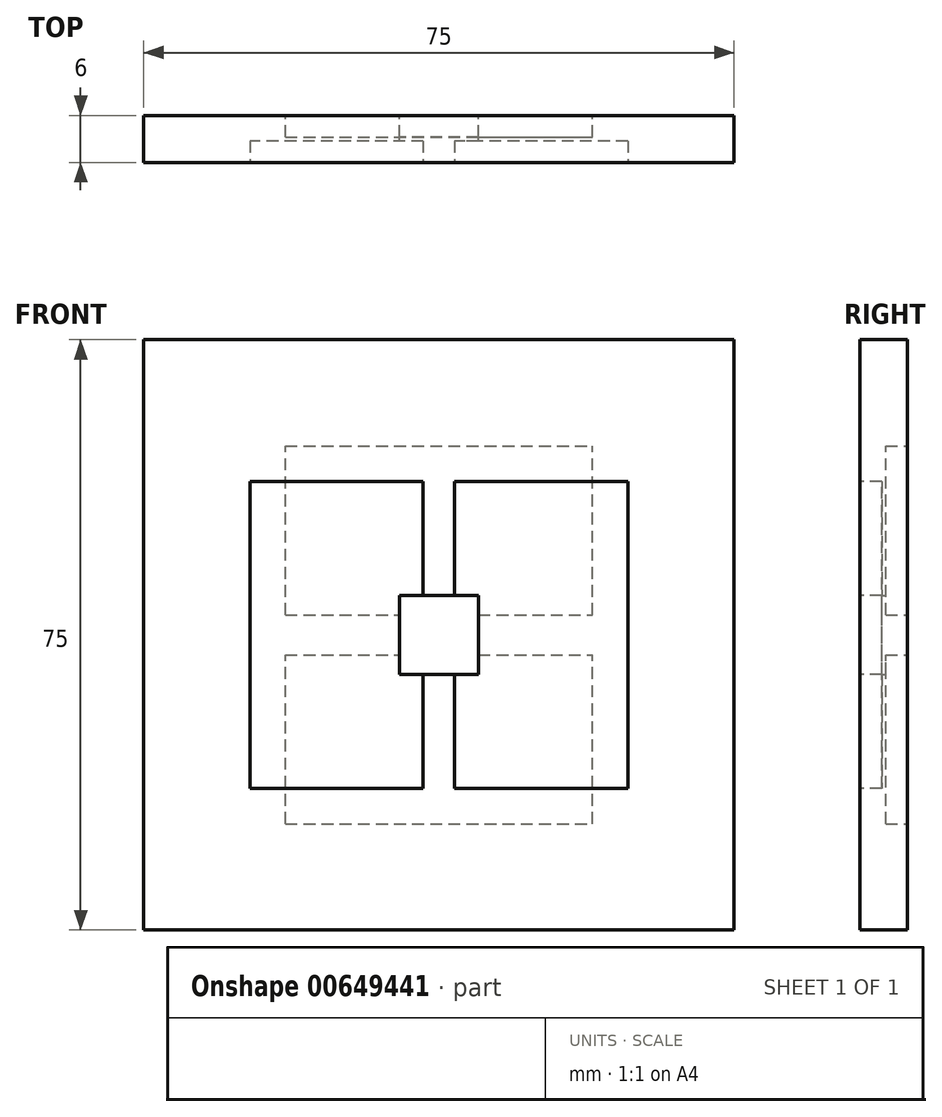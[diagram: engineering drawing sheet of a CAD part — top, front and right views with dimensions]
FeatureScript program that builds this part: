
annotation { "Feature Type Name" : "Feature", "Feature Type Description" : "" }
export const myFeature = defineFeature(function(context is Context, id is Id, definition is map)
    precondition{}
    {
        {
            var Q0;
            Q0=qCreatedBy(makeId("Front.planeOp"),FACE);
            var sketch = newSketch(context, id + "F0", { "sketchPlane" : qUnion([Q0])});
            skLineSegment(sketch, "E0.bottom", {"start": v(37.5, -37.5) * mm, "end": v(-37.5, -37.5) * mm});
            skLineSegment(sketch, "E0.top", {"start": v(37.5, 37.5) * mm, "end": v(-37.5, 37.5) * mm});
            skLineSegment(sketch, "E0.left", {"start": v(37.5, -37.5) * mm, "end": v(37.5, 37.5) * mm});
            skLineSegment(sketch, "E0.right", {"start": v(-37.5, -37.5) * mm, "end": v(-37.5, 37.5) * mm});
            skPoint(sketch, "E0.middle", {"position": v(0, 0) * mm});
            skLineSegment(sketch, "E1.bottom", {"start": v(5, -5) * mm, "end": v(-5, -5) * mm});
            skLineSegment(sketch, "E1.top", {"start": v(5, 5) * mm, "end": v(-5, 5) * mm});
            skLineSegment(sketch, "E1.left", {"start": v(5, -5) * mm, "end": v(5, 5) * mm});
            skLineSegment(sketch, "E1.right", {"start": v(-5, -5) * mm, "end": v(-5, 5) * mm});
            skSolve(sketch);
        }
        {
            var Q0;
            Q0=makeQuery(id+"F0.imprint","IMPRINT",FACE,{"disambiguationData":[TD([[makeQuery(id+"F0.imprint","IMPRINT",EDGE,{"derivedFrom":sQuery(id+"F0.wireOp",EDGE,"odEYJAU4-LrKi-qXot-JqOU-7tA5ZjuLVPrY")}),-1.0]])]});
            var Q1;
            Q1=makeQuery(id+"F0.imprint","IMPRINT",FACE,{"disambiguationData":[TD([[makeQuery(id+"F0.imprint","IMPRINT",EDGE,{"derivedFrom":sQuery(id+"F0.wireOp",EDGE,"E0.bottom")}),-1.0]])]});
            extrude(context, id + "F1", {"entities" : qUnion([Q0, Q1]), "depth" : 6 * mm, "offsetDistance" : 25 * mm});
        }
        {
            var Q0;
            Q0=makeQuery(id+"F1.opExtrude","CAP_FACE",FACE,{"disambiguationData":[OSD([sQuery(id+"F0.wireOp",EDGE,"odEYJAU4-LrKi-qXot-JqOU-7tA5ZjuLVPrY"),sQuery(id+"F0.wireOp",EDGE,"E0.bottom"),sQuery(id+"F0.wireOp",EDGE,"E0.top"),sQuery(id+"F0.wireOp",EDGE,"E0.left"),sQuery(id+"F0.wireOp",EDGE,"E0.right")])],"isStart":false});
            var sketch = newSketch(context, id + "F2", { "sketchPlane" : qUnion([Q0])});
            skLineSegment(sketch, "E2.bottom", {"start": v(24, -19.5) * mm, "end": v(-24, -19.5) * mm});
            skLineSegment(sketch, "E2.top", {"start": v(24, 19.5) * mm, "end": v(-24, 19.5) * mm});
            skLineSegment(sketch, "E2.left", {"start": v(24, -19.5) * mm, "end": v(24, 19.5) * mm});
            skLineSegment(sketch, "E2.right", {"start": v(-24, -19.5) * mm, "end": v(-24, 19.5) * mm});
            skPoint(sketch, "E2.middle", {"position": v(0, 0) * mm});
            skLineSegment(sketch, "E3.bottom", {"start": v(-2, 19.5) * mm, "end": v(2, 19.5) * mm});
            skLineSegment(sketch, "E3.top", {"start": v(-2, -19.5) * mm, "end": v(2, -19.5) * mm});
            skLineSegment(sketch, "E3.left", {"start": v(-2, 19.5) * mm, "end": v(-2, -19.5) * mm});
            skLineSegment(sketch, "E3.right", {"start": v(2, 19.5) * mm, "end": v(2, -19.5) * mm});
            skSolve(sketch);
        }
        {
            var Q0;
            {var subQ0=sQuery(id+"F2.wireOp",EDGE,"E2.right");Q0=makeQuery(id+"F2.imprint","IMPRINT",FACE,{"disambiguationData":[TD([[makeQuery(id+"F2.imprint","IMPRINT",EDGE,{"derivedFrom":subQ0}),-1.0]])]});}
            var Q1;
            {var subQ5=sQuery(id+"F2.wireOp",EDGE,"E2.left");Q1=makeQuery(id+"F2.imprint","IMPRINT",FACE,{"disambiguationData":[TD([[makeQuery(id+"F2.imprint","IMPRINT",EDGE,{"derivedFrom":subQ5}),1.0]])]});}
            extrude(context, id + "F3", {"entities" : qUnion([Q0, Q1]), "operationType" : NewBodyOperationType.REMOVE, "depth" : -2.75 * mm, "offsetDistance" : 25 * mm});
        }
        {
            var Q0;
            Q0=makeQuery(id+"F1.opExtrude","CAP_FACE",FACE,{"disambiguationData":[OSD([sQuery(id+"F0.wireOp",EDGE,"odEYJAU4-LrKi-qXot-JqOU-7tA5ZjuLVPrY"),sQuery(id+"F0.wireOp",EDGE,"E0.bottom"),sQuery(id+"F0.wireOp",EDGE,"E0.top"),sQuery(id+"F0.wireOp",EDGE,"E0.left"),sQuery(id+"F0.wireOp",EDGE,"E0.right")])],"isStart":true});
            var sketch = newSketch(context, id + "F4", { "sketchPlane" : qUnion([Q0])});
            skLineSegment(sketch, "E4.bottom", {"start": v(19.5, -24) * mm, "end": v(-19.5, -24) * mm});
            skLineSegment(sketch, "E4.top", {"start": v(19.5, 24) * mm, "end": v(-19.5, 24) * mm});
            skLineSegment(sketch, "E4.left", {"start": v(19.5, -24) * mm, "end": v(19.5, 24) * mm});
            skLineSegment(sketch, "E4.right", {"start": v(-19.5, -24) * mm, "end": v(-19.5, 24) * mm});
            skPoint(sketch, "E4.middle", {"position": v(0, 0) * mm});
            skLineSegment(sketch, "E5.bottom", {"start": v(19.5, -2.53) * mm, "end": v(-19.5, -2.53) * mm});
            skLineSegment(sketch, "E5.top", {"start": v(19.5, 2.53) * mm, "end": v(-19.5, 2.53) * mm});
            skLineSegment(sketch, "E5.left", {"start": v(19.5, -2.53) * mm, "end": v(19.5, 2.53) * mm});
            skLineSegment(sketch, "E5.right", {"start": v(-19.5, -2.53) * mm, "end": v(-19.5, 2.53) * mm});
            skSolve(sketch);
        }
        {
            var Q0;
            Q0=makeQuery(id+"F4.imprint","IMPRINT",FACE,{"disambiguationData":[TD([[makeQuery(id+"F4.imprint","IMPRINT",EDGE,{"derivedFrom":sQuery(id+"F4.wireOp",EDGE,"E4.bottom")}),-1.0]])]});
            var Q1;
            {var subQ6=sQuery(id+"F4.wireOp",EDGE,"E4.top");Q1=makeQuery(id+"F4.imprint","IMPRINT",FACE,{"disambiguationData":[TD([[makeQuery(id+"F4.imprint","IMPRINT",EDGE,{"derivedFrom":subQ6}),1.0]])]});}
            extrude(context, id + "F5", {"entities" : qUnion([Q0, Q1]), "operationType" : NewBodyOperationType.REMOVE, "oppositeDirection" : true, "depth" : 2.75 * mm, "offsetDistance" : 25 * mm});
        }
    });
